# Revit family: Layout-Teknion-Zones_Lounge_01-R2022
name_source: partatom
category: Furniture Systems
units: mm (PartAtom-declared; Revit-internal decimal feet)

## family parameters
Always vertical = Yes
Cut with Voids When Loaded = No
OmniClass Number = 23.40.70.14.64.21
OmniClass Title = Systems Furniture
Part Type = Normal
Room Calculation Point = No
Round Connector Dimension = Use Diameter
Shared = No
Work Plane-Based = No

## types (1)
- Lounge 01
    Assembly Code = E2020200
    Default Elevation = 0' - 0"
    Depth = 4' - 0"
    Description = 4'-0" x 12'-0"
    Height = 5' - 10"
    Manufacturer = Teknion
    Manufacturer Fax = 416.661.4586
    Model = Lounge 01
    Product Line = Zones
    Product Page URL = http://teknionplanningtool.com
    Series = Zones
    Stool Seat Wood Finish Note = Same as Stool Wood Frame Finish
    Sustainability Data = http://www.teknion.com
    URL = www.teknion.com
    Warranty = http://www.teknion.com
    Width = 12' - 0"

## geometry (parser evidence)
native form markers: Blend x45, Sweep x15
no freeform markers — native parametric forms only
